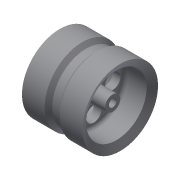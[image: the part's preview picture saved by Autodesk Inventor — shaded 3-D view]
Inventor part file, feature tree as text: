
AUTODESK INVENTOR PART (.ipt)
format: ipt  version: 2015 (Build 190159000, 159)  size: 185,856 bytes
history: native  units: mm
features: sketch x5, hole x3, revolve x1
ambient origin geometry x8: Origin, YZ Plane, XZ Plane, XY Plane, X Axis, Y Axis, Z Axis, Center Point
bodies: Solid1 (feature_tree)
feature tree (9):
  revolve  "Revolution1"  [1 undecoded]
  hole  "Hole1"  [1 undecoded]
  hole  "Hole2"  [1 undecoded]
  sketch  "Sketch4"  dims[d14=90.0deg d15=3.0mm]
  hole  "Hole3"  [1 undecoded]
  sketch  "Sketch1"  dims[d0=6.0mm d1=2.0mm]
  sketch  "Sketch2"  dims[d3=5.0mm d6=12.0mm]
  sketch  "Sketch3"  dims[d7=2.0mm d8=5.0mm]
  sketch  "Sketch5"  dims[d16=3.0mm d17=3.0mm d18=3.0mm d19=5.0mm d20=6.0mm d21=4.0mm d22=2.0mm d23=90.0deg d24=8.0mm d25=0.0mm d26=5.0mm d27=5.0mm d28=6.0mm d29=5.0mm d30=5.0mm d31=3.0mm d32=3.0mm d33=3.0mm d34=3.0mm d35=4.0mm d36=6.0mm d37=4.0mm d38=2.0mm d39=90.0deg d40=8.0mm d41=0.0mm d42=2.0mm d43=6.0mm d44=4.0mm d45=2.0mm d46=90.0deg d47=20.0mm d48=0.0mm d49=2.0mm d50=1.0mm d51=4.0mm]
note: 4 required parameter values undecoded (feature->parameter linkage not recoverable at this tier; creation-order binding heuristic only, values carry confidence <= 0.55)